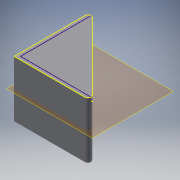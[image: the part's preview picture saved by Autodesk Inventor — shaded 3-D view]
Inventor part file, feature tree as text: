
AUTODESK INVENTOR PART (.ipt)
format: ipt  version: 2019 (Build 230136000, 136)  size: 108,032 bytes
history: native  units: mm
features: other x2, sketch x2, extrude x1, projected_geometry x1
ambient origin geometry x8: Origin, YZ Plane, XZ Plane, XY Plane, X Axis, Y Axis, Z Axis, Center Point
bodies: Body1 (feature_tree)
feature tree (6):
  other  "솔리드1"
  extrude  "돌출1"  Depth=25.0mm
  other  "작업 평면1"
  sketch  "스케치4"
  sketch  "스케치2"
  projected_geometry  "투영된 루프2"
